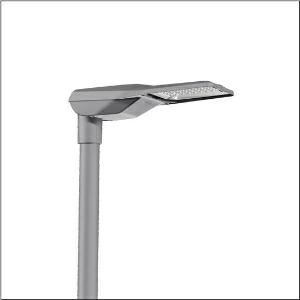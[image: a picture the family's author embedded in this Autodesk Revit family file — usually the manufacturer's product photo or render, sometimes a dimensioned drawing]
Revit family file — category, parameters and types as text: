
# Revit family: streetlight_sl_21_iq_mini___stw1_0a_5xe2e21d08hb_2a42
name_source: partatom
category: Lighting Fixtures
units: mm (PartAtom-declared; Revit-internal decimal feet)

## family parameters
Cut with Voids When Loaded = No
Host = Face
Light Source = No
Part Type = Normal
Room Calculation Point = No
Round Connector Dimension = Use Diameter
Shared = No

## types (1)
- --- (1 x LED, 7830 lm, 70.9 W, 2200K)
    Apparent Load = 71 VA
    CIE Flux Codes = 38 75 98 100 100
    Color Rendering = 70
    Color Temperature = 2200K
    Default Elevation = 1800 mm
    Description = Streetlight SL 21 iQ mini, mast luminaire, primary light control with lens, of PMMA, primary optical cover: cover, of toughened safety glass, transparent, light distribution: STW1.0a, light emission: direct distribution, primary light characteristic: asymmetric, installation type: post-top, side-entry, LED, High Power LED, rated luminous flux: 7.830lm, luminous efficacy: 110lm/W, light colour: 722, colour temperature: 2200K, control: Auto-Match, Temp-Guard, Lumen-Switch, Night-Set, Smart-Wire, Light-Fading, Desk-Remote (wireless, voltage-free reading and setting of iQ features in the workshop via application-optimized NFC function/RFID function), optimised constant luminous flux control (CLO 2.0), presetting dimming linear, mains connection: 220..240V, AC, 50/60Hz, start of lifetime: 71W, end of service life: 75W, reduction: 31W, luminaire housing, of diecast aluminium, powder-coated, Siteco® metallic grey (DB 702S), corrosivity category C5 mid according to DIN EN ISO 12944, please order mast flange separately, inclination adjustable: 0°, 5°, 10°, 15°, sealing non-destructively replaceable, multi-level sealing system, length: 628mm, width: 235mm, height: 110mm, mast flange for spigot size: 42mm (side-entry): 5XC10008XM4, 60/48mm (side-entry/post-top): 5XC10108XM2, 76/60mm (side-entry/post-top): 5XC10108XM1, protection rating (complete): IP66, insulation class (complete): insulation class II (safety insulation), certification: CE, ENEC, ENEC+, VDE, impact resistance: IK09, permissible operating ambient temperature for outdoor applications: -40..+50°C, standard-compliant lighting for roads and squares, packaging unit: 1 piece

Light Distribution: STW1.0a
    Height = 110 mm
    Lamp = 1 x LED
    Lamp Light Flux = 7830 lm
    Lamp Power = 70.9 W
    Lamp count = 1
    Length = 625 mm
    Luminous efficacy = 110 lm/W
    Manufacturer = Siteco
    ModVariant = No
    Model = 5XE2E21D08HB
    Number of Poles = 1
    OnlyDefault = Yes
    Power Factor = 1
    Product Name = Streetlight SL 21 iQ mini | STW1.0a
    Product group = mast luminaire | pylon top
    ProductGroupID = 6100
    Protection Class = Protection class II
    Protection Degree = IP 66
    RLX_Detail_Level = 1
    RLX_Emergency_Light_Flux = 0 lm
    RLX_Emergency_Type = 0
    RLX_Emergency_Type_DB = No
    RlxData = <blob elided: 92225 chars, md5=bb467a1f>
    Socket = socket
    Standby Power = 0 W
    System Light Flux = 7830 lm
    System Power = 71 W
    Type Comments = factory setting: luminous flux: 100 % | dim-lin: 254 | 711 mA
    Type Image = l_1003519.jpg
    URL = http://relux.com
    VarID = @adj_090343
    Voltage = 0 V
    Weight = 0.00 kg
    Width = 234 mm

## geometry (parser evidence)
native form markers: Blend x4, Sweep x11
no freeform markers — native parametric forms only
